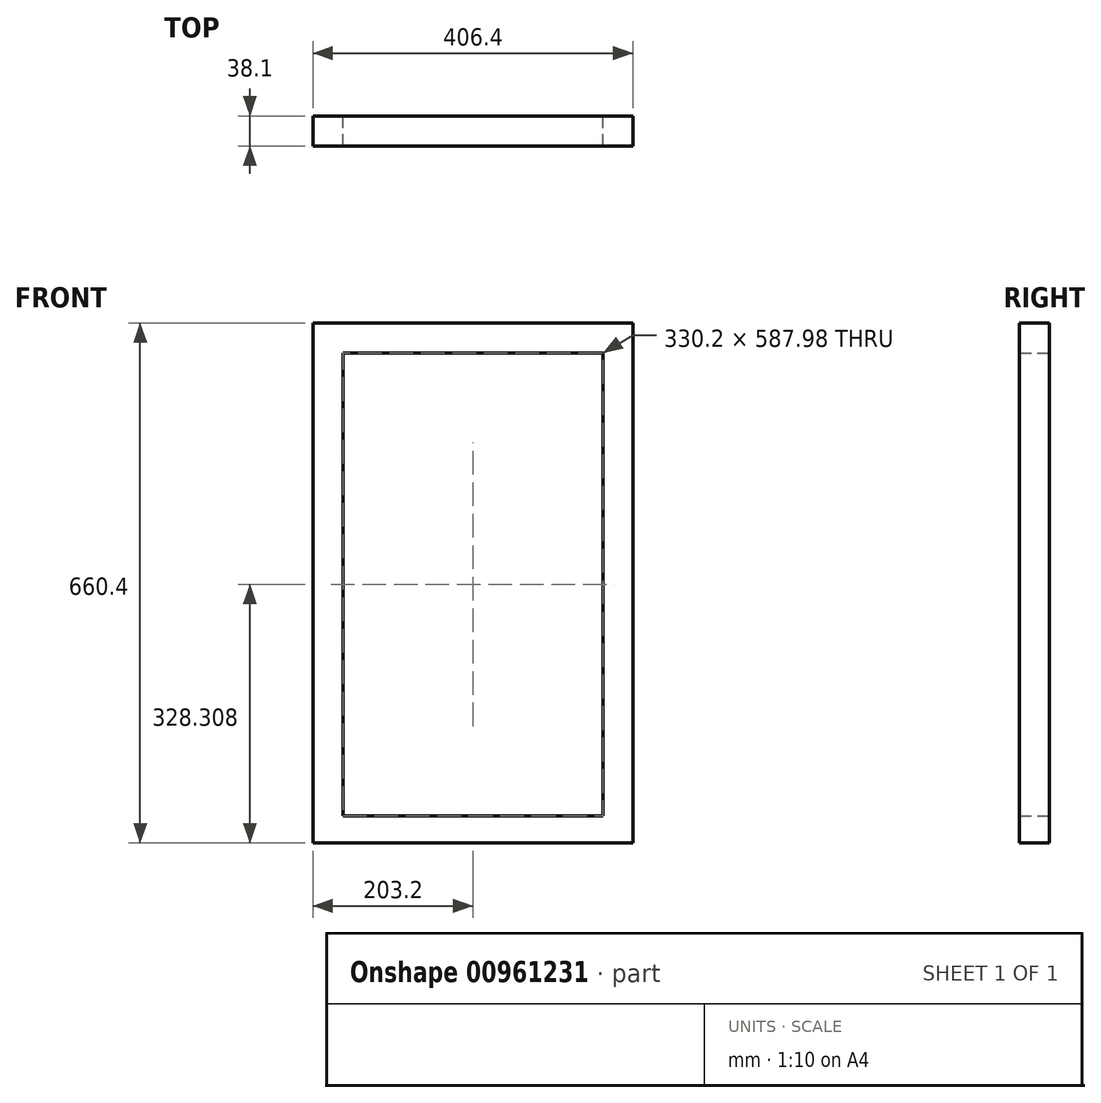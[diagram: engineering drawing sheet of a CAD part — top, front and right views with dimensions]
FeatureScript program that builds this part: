
annotation { "Feature Type Name" : "Feature", "Feature Type Description" : "" }
export const myFeature = defineFeature(function(context is Context, id is Id, definition is map)
    precondition{}
    {
        {
            var Q0;
            Q0=qCreatedBy(makeId("Top.planeOp"),FACE);
            var sketch = newSketch(context, id + "F0", { "sketchPlane" : qUnion([Q0])});
            skLineSegment(sketch, "E0.bottom", {"start": v(19.05, 19.05) * mm, "end": v(-19.05, 19.05) * mm});
            skLineSegment(sketch, "E0.top", {"start": v(19.05, -19.05) * mm, "end": v(-19.05, -19.05) * mm});
            skLineSegment(sketch, "E0.left", {"start": v(19.05, 19.05) * mm, "end": v(19.05, -19.05) * mm});
            skLineSegment(sketch, "E0.right", {"start": v(-19.05, 19.05) * mm, "end": v(-19.05, -19.05) * mm});
            skPoint(sketch, "E0.middle", {"position": v(0, 0) * mm});
            skSolve(sketch);
        }
        {
            var Q0;
            Q0 = qSketchRegion(id + "F0", true);
            extrude(context, id + "F1", {"entities" : qUnion([Q0]), "depth" : 660.4 * mm, "offsetDistance" : 25.4 * mm});
        }
        {
            var Q0;
            Q0=makeQuery(id+"F1.opExtrude","SWEPT_FACE",FACE,{"disambiguationData":[OSD([sQuery(id+"F0.wireOp",EDGE,"E0.left")])]});
            var sketch = newSketch(context, id + "F2", { "sketchPlane" : qUnion([Q0])});
            skLineSegment(sketch, "E1.bottom", {"start": v(-19.05, 660.4) * mm, "end": v(19.05, 660.4) * mm});
            skLineSegment(sketch, "E1.top", {"start": v(-19.05, 622.3) * mm, "end": v(19.05, 622.3) * mm});
            skLineSegment(sketch, "E1.left", {"start": v(-19.05, 660.4) * mm, "end": v(-19.05, 622.3) * mm});
            skLineSegment(sketch, "E1.right", {"start": v(19.05, 660.4) * mm, "end": v(19.05, 622.3) * mm});
            skSolve(sketch);
        }
        {
            var Q0;
            Q0=makeQuery(id+"F2.imprint","IMPRINT",FACE,{"disambiguationData":[TD([[makeQuery(id+"F2.imprint","IMPRINT",EDGE,{"derivedFrom":sQuery(id+"F2.wireOp",EDGE,"E1.bottom")}),1.0]])]});
            extrude(context, id + "F3", {"entities" : qUnion([Q0]), "operationType" : NewBodyOperationType.ADD, "depth" : 330.2 * mm, "offsetDistance" : 25.4 * mm});
        }
        {
            var Q0;
            Q0=makeQuery(id+"F1.opExtrude","SWEPT_FACE",FACE,{"disambiguationData":[OSD([sQuery(id+"F0.wireOp",EDGE,"E0.left")])]});
            var sketch = newSketch(context, id + "F4", { "sketchPlane" : qUnion([Q0])});
            skLineSegment(sketch, "E2.bottom", {"start": v(-19.05, 0) * mm, "end": v(19.05, 0) * mm});
            skLineSegment(sketch, "E2.top", {"start": v(-19.05, 34.32) * mm, "end": v(19.05, 34.32) * mm});
            skLineSegment(sketch, "E2.left", {"start": v(-19.05, 0) * mm, "end": v(-19.05, 34.32) * mm});
            skLineSegment(sketch, "E2.right", {"start": v(19.05, 0) * mm, "end": v(19.05, 34.32) * mm});
            skSolve(sketch);
        }
        {
            var Q0;
            Q0=makeQuery(id+"F4.imprint","IMPRINT",FACE,{"disambiguationData":[TD([[makeQuery(id+"F4.imprint","IMPRINT",EDGE,{"derivedFrom":sQuery(id+"F4.wireOp",EDGE,"E2.bottom")}),-1.0]])]});
            extrude(context, id + "F5", {"entities" : qUnion([Q0]), "operationType" : NewBodyOperationType.ADD, "depth" : 330.2 * mm, "offsetDistance" : 25.4 * mm});
        }
        {
            var Q0;
            Q0=makeQuery(id+"F5.boolean.opBoolean","MERGE",FACE,{"derivedFrom":[makeQuery(id+"F1.opExtrude","CAP_FACE",FACE,{"disambiguationData":[OSD([sQuery(id+"F0.wireOp",EDGE,"E0.bottom"),sQuery(id+"F0.wireOp",EDGE,"E0.top"),sQuery(id+"F0.wireOp",EDGE,"E0.left"),sQuery(id+"F0.wireOp",EDGE,"E0.right")])],"isStart":true}),makeQuery(id+"F5.opExtrude","SWEPT_FACE",FACE,{"disambiguationData":[OSD([sQuery(id+"F4.wireOp",EDGE,"E2.bottom")])]})]});
            var sketch = newSketch(context, id + "F6", { "sketchPlane" : qUnion([Q0])});
            skLineSegment(sketch, "E3", {"start": v(349.25, 19.05) * mm, "end": v(349.25, -19.05) * mm});
            skLineSegment(sketch, "E4", {"start": v(349.25, -19.05) * mm, "end": v(387.35, -19.05) * mm});
            skLineSegment(sketch, "E5", {"start": v(387.35, -19.05) * mm, "end": v(387.35, 19.05) * mm});
            skLineSegment(sketch, "E6", {"start": v(387.35, 19.05) * mm, "end": v(349.25, 19.05) * mm});
            skSolve(sketch);
        }
        {
            var Q0;
            Q0=makeQuery(id+"F6.imprint","IMPRINT",FACE,{"disambiguationData":[TD([[makeQuery(id+"F6.imprint","IMPRINT",EDGE,{"derivedFrom":sQuery(id+"F6.wireOp",EDGE,"E3")}),-1.0]])]});
            extrude(context, id + "F7", {"entities" : qUnion([Q0]), "operationType" : NewBodyOperationType.ADD, "oppositeDirection" : true, "depth" : 660.4 * mm, "offsetDistance" : 25.4 * mm});
        }
    });
